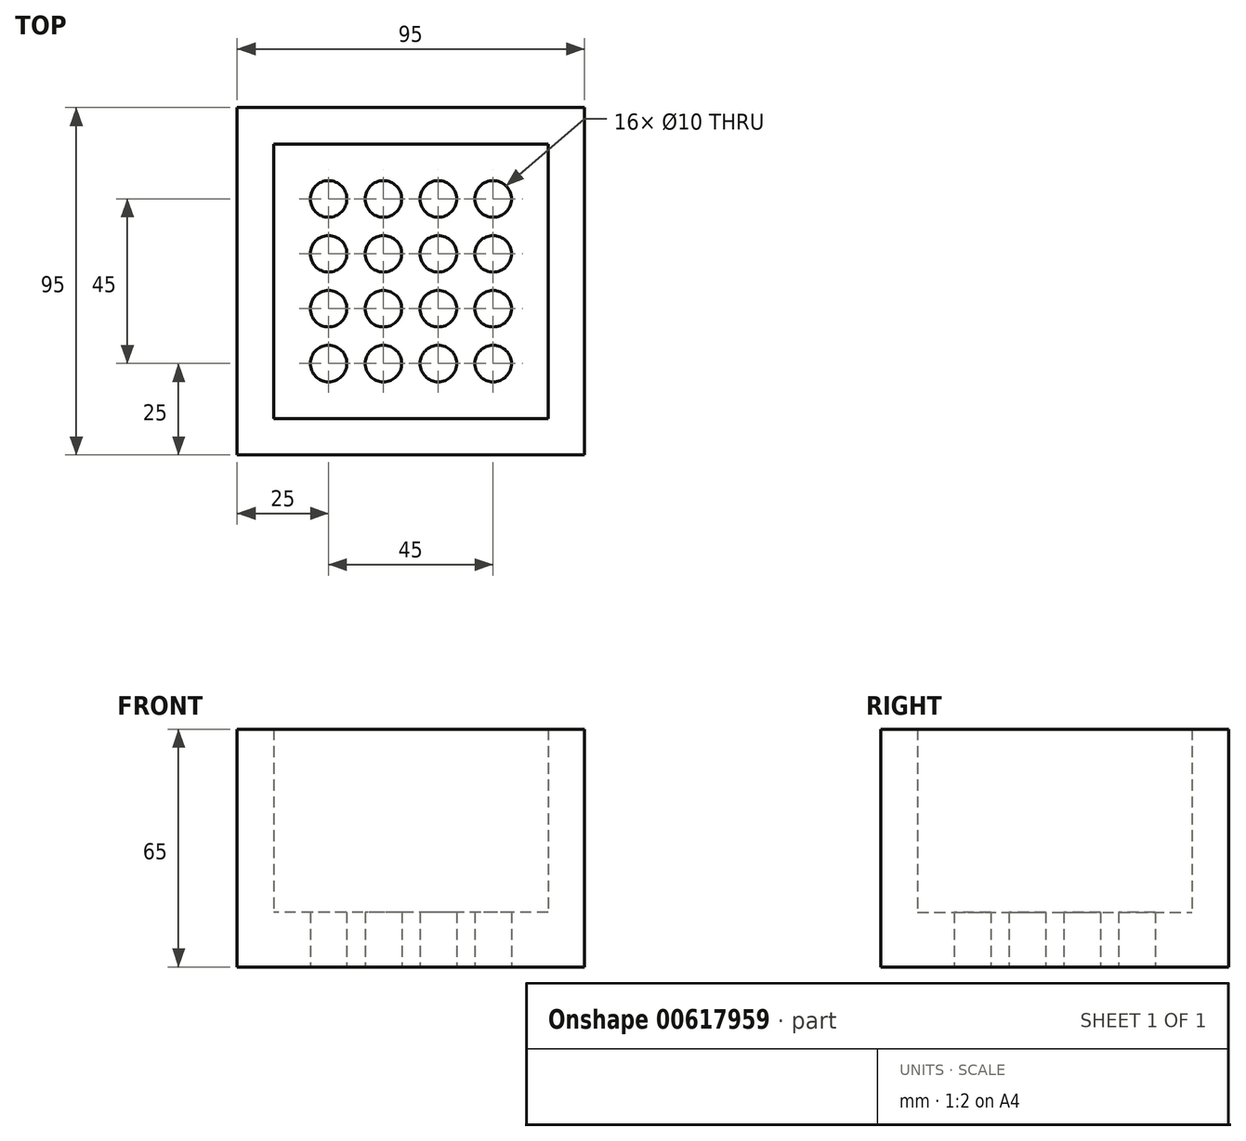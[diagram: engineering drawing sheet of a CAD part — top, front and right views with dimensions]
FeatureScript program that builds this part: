
annotation { "Feature Type Name" : "Feature", "Feature Type Description" : "" }
export const myFeature = defineFeature(function(context is Context, id is Id, definition is map)
    precondition{}
    {
        {
            var Q0;
            Q0=qCreatedBy(makeId("Top.planeOp"),FACE);
            var sketch = newSketch(context, id + "F0", { "sketchPlane" : qUnion([Q0])});
            skCircle(sketch, "E0", {"center": v(25, 25) * mm, "radius": 5 * mm});
            skCircle(sketch, "E1.0.1.0", {"center": v(25, 40) * mm, "radius": 5 * mm});
            skCircle(sketch, "E1.0.2.0", {"center": v(25, 55) * mm, "radius": 5 * mm});
            skCircle(sketch, "E1.0.3.0", {"center": v(25, 70) * mm, "radius": 5 * mm});
            skCircle(sketch, "E1.1.0.0", {"center": v(40, 25) * mm, "radius": 5 * mm});
            skCircle(sketch, "E1.1.1.0", {"center": v(40, 40) * mm, "radius": 5 * mm});
            skCircle(sketch, "E1.1.2.0", {"center": v(40, 55) * mm, "radius": 5 * mm});
            skCircle(sketch, "E1.1.3.0", {"center": v(40, 70) * mm, "radius": 5 * mm});
            skCircle(sketch, "E1.2.0.0", {"center": v(55, 25) * mm, "radius": 5 * mm});
            skCircle(sketch, "E1.2.1.0", {"center": v(55, 40) * mm, "radius": 5 * mm});
            skCircle(sketch, "E1.2.2.0", {"center": v(55, 55) * mm, "radius": 5 * mm});
            skCircle(sketch, "E1.2.3.0", {"center": v(55, 70) * mm, "radius": 5 * mm});
            skCircle(sketch, "E1.3.0.0", {"center": v(70, 25) * mm, "radius": 5 * mm});
            skCircle(sketch, "E1.3.1.0", {"center": v(70, 40) * mm, "radius": 5 * mm});
            skCircle(sketch, "E1.3.2.0", {"center": v(70, 55) * mm, "radius": 5 * mm});
            skCircle(sketch, "E1.3.3.0", {"center": v(70, 70) * mm, "radius": 5 * mm});
            skLineSegment(sketch, "E1.direction1", {"start": v(25, 25) * mm, "end": v(40, 25) * mm, "construction": true});
            skLineSegment(sketch, "E1.direction2", {"start": v(25, 25) * mm, "end": v(25, 40) * mm, "construction": true});
            skLineSegment(sketch, "E2.bottom", {"start": v(0, 0) * mm, "end": v(95, 0) * mm});
            skLineSegment(sketch, "E2.top", {"start": v(0, 95) * mm, "end": v(95, 95) * mm});
            skLineSegment(sketch, "E2.left", {"start": v(0, 0) * mm, "end": v(0, 95) * mm});
            skLineSegment(sketch, "E2.right", {"start": v(95, 0) * mm, "end": v(95, 95) * mm});
            skLineSegment(sketch, "E3.bottom", {"start": v(110, -42.78) * mm, "end": v(110, -42.78) * mm});
            skLineSegment(sketch, "E3.top", {"start": v(110, -56.31) * mm, "end": v(110, -56.31) * mm});
            skSolve(sketch);
        }
        {
            var Q0;
            Q0 = qSketchRegion(id + "F0", true);
            extrude(context, id + "F1", {"entities" : qUnion([Q0]), "depth" : 15 * mm, "offsetDistance" : 25 * mm});
        }
        {
            var Q0;
            Q0=makeQuery(id+"F1.opExtrude","CAP_FACE",FACE,{"disambiguationData":[OSD([sQuery(id+"F0.wireOp",EDGE,"E0"),sQuery(id+"F0.wireOp",EDGE,"E1.0.1.0"),sQuery(id+"F0.wireOp",EDGE,"E1.0.2.0"),sQuery(id+"F0.wireOp",EDGE,"E1.0.3.0"),sQuery(id+"F0.wireOp",EDGE,"E1.1.0.0"),sQuery(id+"F0.wireOp",EDGE,"E1.1.1.0"),sQuery(id+"F0.wireOp",EDGE,"E1.1.2.0"),sQuery(id+"F0.wireOp",EDGE,"E1.1.3.0"),sQuery(id+"F0.wireOp",EDGE,"E1.2.0.0"),sQuery(id+"F0.wireOp",EDGE,"E1.2.1.0"),sQuery(id+"F0.wireOp",EDGE,"E1.2.2.0"),sQuery(id+"F0.wireOp",EDGE,"E1.2.3.0"),sQuery(id+"F0.wireOp",EDGE,"E1.3.0.0"),sQuery(id+"F0.wireOp",EDGE,"E1.3.1.0"),sQuery(id+"F0.wireOp",EDGE,"E1.3.2.0"),sQuery(id+"F0.wireOp",EDGE,"E1.3.3.0"),sQuery(id+"F0.wireOp",EDGE,"E2.bottom"),sQuery(id+"F0.wireOp",EDGE,"E2.top"),sQuery(id+"F0.wireOp",EDGE,"E2.left"),sQuery(id+"F0.wireOp",EDGE,"E2.right")])],"isStart":false});
            var sketch = newSketch(context, id + "F2", { "sketchPlane" : qUnion([Q0])});
            skLineSegment(sketch, "E4.0", {"start": v(85, 85) * mm, "end": v(10, 85) * mm});
            skLineSegment(sketch, "E4.1", {"start": v(85, 10) * mm, "end": v(85, 85) * mm});
            skLineSegment(sketch, "E4.2", {"start": v(10, 10) * mm, "end": v(85, 10) * mm});
            skLineSegment(sketch, "E4.3", {"start": v(10, 85) * mm, "end": v(10, 10) * mm});
            skSolve(sketch);
        }
        {
            var Q0;
            Q0=makeQuery(id+"F2.imprint","IMPRINT",FACE,{"disambiguationData":[TD([[makeQuery(id+"F2.imprint","IMPRINT",EDGE,{"derivedFrom":sQuery(id+"F2.wireOp",EDGE,"E4.0")}),-1.0]])]});
            extrude(context, id + "F3", {"entities" : qUnion([Q0]), "operationType" : NewBodyOperationType.ADD, "depth" : 50 * mm, "offsetDistance" : 25 * mm});
        }
    });
